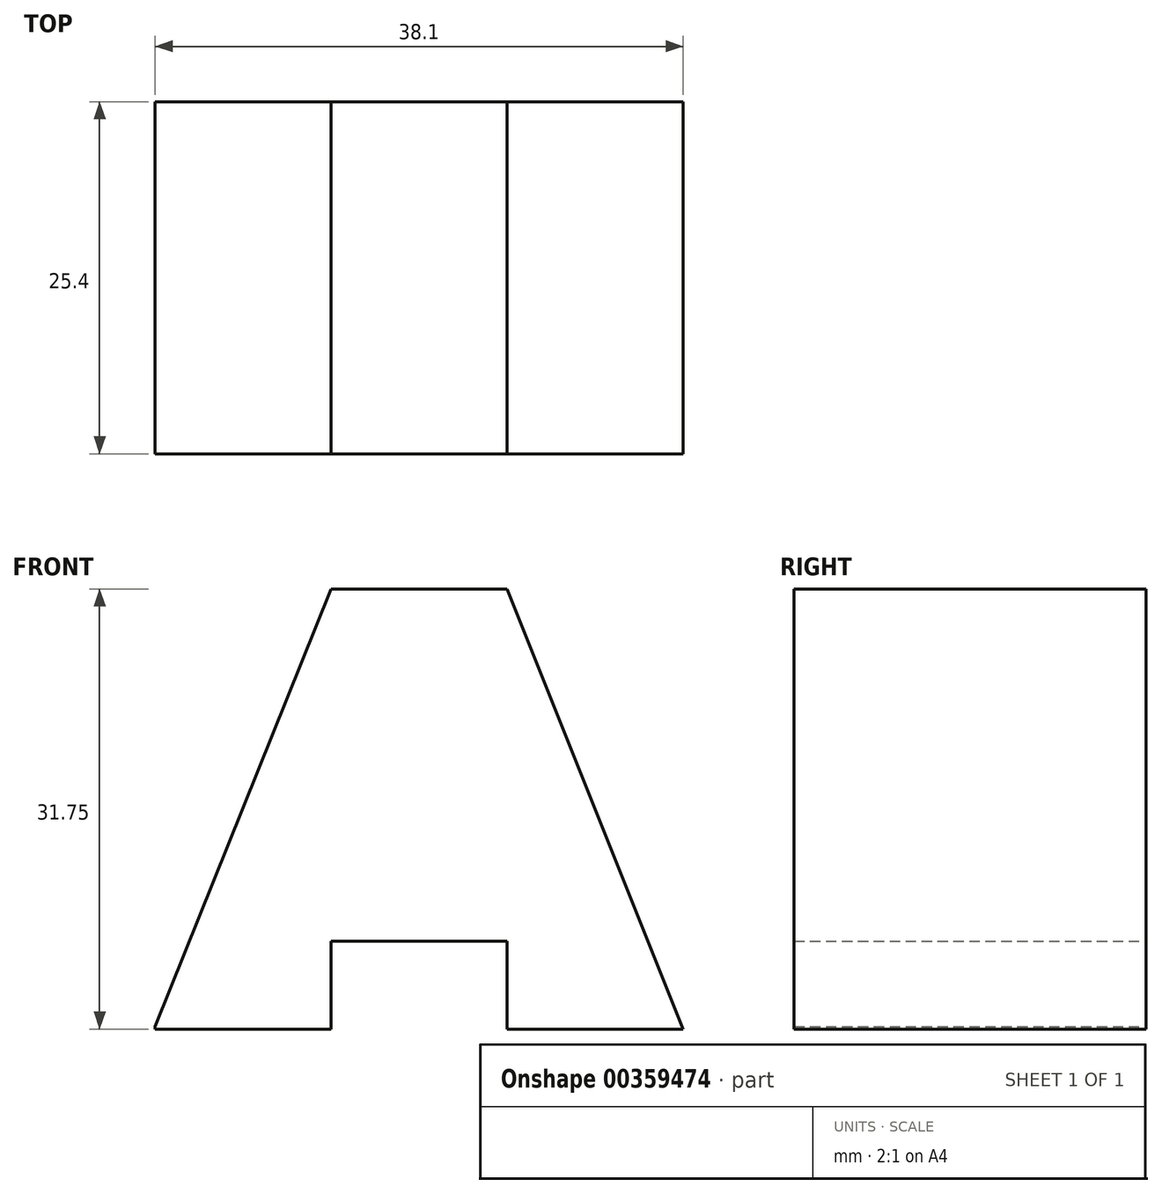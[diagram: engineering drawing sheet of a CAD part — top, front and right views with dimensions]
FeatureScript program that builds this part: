
annotation { "Feature Type Name" : "Feature", "Feature Type Description" : "" }
export const myFeature = defineFeature(function(context is Context, id is Id, definition is map)
    precondition{}
    {
        {
            var Q0;
            Q0=qCreatedBy(makeId("Front.planeOp"),FACE);
            var sketch = newSketch(context, id + "F0", { "sketchPlane" : qUnion([Q0])});
            skLineSegment(sketch, "E0", {"start": v(13.14, 34.88) * mm, "end": v(13.14, 3.13) * mm});
            skLineSegment(sketch, "E1", {"start": v(13.14, 3.13) * mm, "end": v(51.24, 3.13) * mm});
            skLineSegment(sketch, "E2", {"start": v(51.24, 3.13) * mm, "end": v(51.24, 34.88) * mm});
            skLineSegment(sketch, "E3", {"start": v(51.24, 34.88) * mm, "end": v(13.14, 34.88) * mm});
            skSolve(sketch);
        }
        {
            var Q0;
            Q0=makeQuery(id+"F0.imprint","IMPRINT",FACE,{"disambiguationData":[TD([[makeQuery(id+"F0.imprint","IMPRINT",EDGE,{"derivedFrom":sQuery(id+"F0.wireOp",EDGE,"E0")}),1.0]])]});
            extrude(context, id + "F1", {"entities" : qUnion([Q0]), "depth" : 25.4 * mm});
        }
        {
            var Q0;
            Q0=qCreatedBy(makeId("Front.planeOp"),FACE);
            var sketch = newSketch(context, id + "F2", { "sketchPlane" : qUnion([Q0])});
            skLineSegment(sketch, "E4", {"start": v(38.54, 34.88) * mm, "end": v(51.24, 3.13) * mm});
            skLineSegment(sketch, "E5", {"start": v(51.24, 34.88) * mm, "end": v(51.24, 3.13) * mm});
            skLineSegment(sketch, "E6", {"start": v(51.24, 34.88) * mm, "end": v(38.54, 34.88) * mm});
            skSolve(sketch);
        }
        {
            var Q0;
            Q0 = qSketchRegion(id + "F2", true);
            extrude(context, id + "F3", {"entities" : qUnion([Q0]), "operationType" : NewBodyOperationType.REMOVE, "depth" : 25.4 * mm});
        }
        {
            var Q0;
            Q0=qCreatedBy(makeId("Front.planeOp"),FACE);
            var sketch = newSketch(context, id + "F4", { "sketchPlane" : qUnion([Q0])});
            skLineSegment(sketch, "E7", {"start": v(25.84, 34.88) * mm, "end": v(13.14, 3.3) * mm});
            skLineSegment(sketch, "E8", {"start": v(13.14, 3.3) * mm, "end": v(13.14, 35.06) * mm});
            skLineSegment(sketch, "E9", {"start": v(13.14, 35.06) * mm, "end": v(25.84, 34.88) * mm});
            skSolve(sketch);
        }
        {
            var Q0;
            Q0 = qSketchRegion(id + "F4", true);
            extrude(context, id + "F5", {"entities" : qUnion([Q0]), "operationType" : NewBodyOperationType.REMOVE, "depth" : 25.4 * mm});
        }
        {
            var Q0;
            Q0=qCreatedBy(makeId("Front.planeOp"),FACE);
            var sketch = newSketch(context, id + "F6", { "sketchPlane" : qUnion([Q0])});
            skLineSegment(sketch, "E10", {"start": v(25.84, 3.13) * mm, "end": v(25.84, 9.48) * mm});
            skLineSegment(sketch, "E11", {"start": v(25.84, 9.48) * mm, "end": v(38.54, 9.48) * mm});
            skLineSegment(sketch, "E12", {"start": v(38.54, 9.48) * mm, "end": v(38.54, 3.13) * mm});
            skLineSegment(sketch, "E13", {"start": v(25.84, 3.13) * mm, "end": v(38.54, 3.13) * mm});
            skSolve(sketch);
        }
        {
            var Q0;
            Q0 = qSketchRegion(id + "F6", true);
            extrude(context, id + "F7", {"entities" : qUnion([Q0]), "operationType" : NewBodyOperationType.REMOVE, "depth" : 25.4 * mm});
        }
    });
